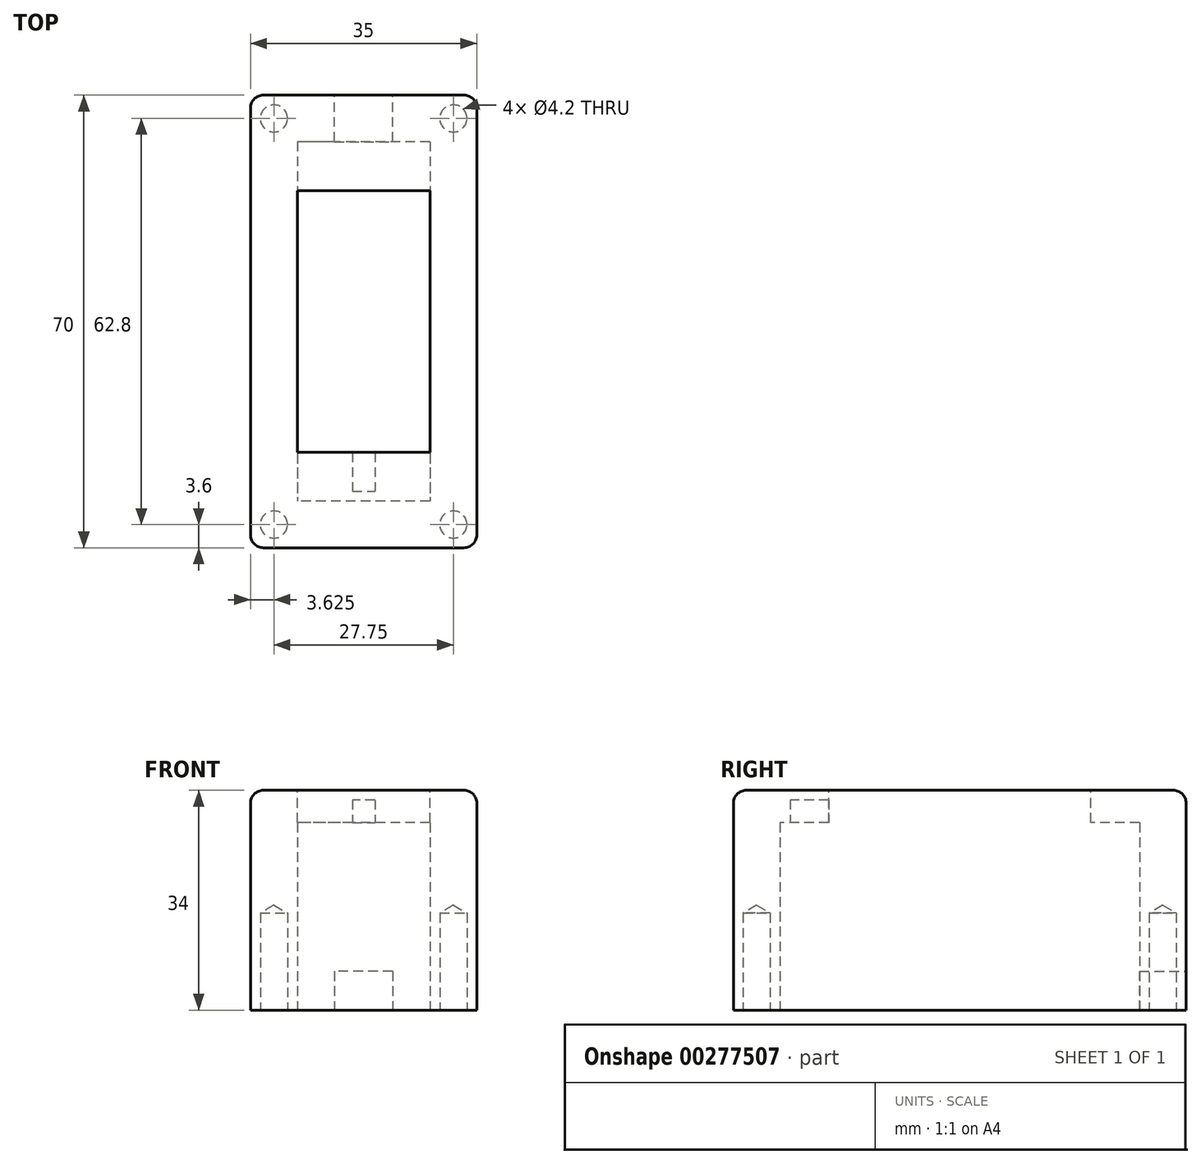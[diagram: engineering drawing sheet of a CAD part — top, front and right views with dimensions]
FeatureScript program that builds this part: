
annotation { "Feature Type Name" : "Feature", "Feature Type Description" : "" }
export const myFeature = defineFeature(function(context is Context, id is Id, definition is map)
    precondition{}
    {
        {
            var Q0;
            Q0=qCreatedBy(makeId("Top.planeOp"),FACE);
            var sketch = newSketch(context, id + "F0", { "sketchPlane" : qUnion([Q0])});
            skLineSegment(sketch, "E0.bottom", {"start": v(17.5, 35) * mm, "end": v(-17.5, 35) * mm});
            skLineSegment(sketch, "E0.top", {"start": v(17.5, -35) * mm, "end": v(-17.5, -35) * mm});
            skLineSegment(sketch, "E0.left", {"start": v(17.5, 35) * mm, "end": v(17.5, -35) * mm});
            skLineSegment(sketch, "E0.right", {"start": v(-17.5, 35) * mm, "end": v(-17.5, -35) * mm});
            skPoint(sketch, "E0.middle", {"position": v(0, 0) * mm});
            skSolve(sketch);
        }
        {
            var Q0;
            Q0=makeQuery(id+"F0.imprint","IMPRINT",FACE,{"disambiguationData":[TD([[makeQuery(id+"F0.imprint","IMPRINT",EDGE,{"derivedFrom":sQuery(id+"F0.wireOp",EDGE,"E0.bottom")}),1.0]])]});
            extrude(context, id + "F1", {"entities" : qUnion([Q0]), "depth" : 40 * mm});
        }
        {
            var Q0;
            Q0=makeQuery(id+"F1.opExtrude","CAP_FACE",FACE,{"disambiguationData":[OSD([sQuery(id+"F0.wireOp",EDGE,"E0.bottom"),sQuery(id+"F0.wireOp",EDGE,"E0.top"),sQuery(id+"F0.wireOp",EDGE,"E0.left"),sQuery(id+"F0.wireOp",EDGE,"E0.right")])],"isStart":true});
            var sketch = newSketch(context, id + "F2", { "sketchPlane" : qUnion([Q0])});
            skLineSegment(sketch, "E1.bottom", {"start": v(10.25, -27.8) * mm, "end": v(-10.25, -27.8) * mm});
            skLineSegment(sketch, "E1.top", {"start": v(10.25, 27.8) * mm, "end": v(-10.25, 27.8) * mm});
            skLineSegment(sketch, "E1.left", {"start": v(10.25, -27.8) * mm, "end": v(10.25, 27.8) * mm});
            skLineSegment(sketch, "E1.right", {"start": v(-10.25, -27.8) * mm, "end": v(-10.25, 27.8) * mm});
            skPoint(sketch, "E1.middle", {"position": v(0, 0) * mm});
            skSolve(sketch);
        }
        {
            var Q0;
            Q0=makeQuery(id+"F2.imprint","IMPRINT",FACE,{"disambiguationData":[TD([[makeQuery(id+"F2.imprint","IMPRINT",EDGE,{"derivedFrom":sQuery(id+"F2.wireOp",EDGE,"E1.bottom")}),-1.0]])]});
            extrude(context, id + "F3", {"entities" : qUnion([Q0]), "operationType" : NewBodyOperationType.REMOVE, "oppositeDirection" : true, "depth" : 35 * mm});
        }
        {
            var Q0;
            Q0=makeQuery(id+"F1.opExtrude","CAP_FACE",FACE,{"disambiguationData":[OSD([sQuery(id+"F0.wireOp",EDGE,"E0.bottom"),sQuery(id+"F0.wireOp",EDGE,"E0.top"),sQuery(id+"F0.wireOp",EDGE,"E0.left"),sQuery(id+"F0.wireOp",EDGE,"E0.right")])],"isStart":false});
            var sketch = newSketch(context, id + "F4", { "sketchPlane" : qUnion([Q0])});
            skLineSegment(sketch, "E2.bottom", {"start": v(-10.25, 20.25) * mm, "end": v(10.25, 20.25) * mm});
            skLineSegment(sketch, "E2.top", {"start": v(-10.25, -20.25) * mm, "end": v(10.25, -20.25) * mm});
            skLineSegment(sketch, "E2.left", {"start": v(-10.25, 20.25) * mm, "end": v(-10.25, -20.25) * mm});
            skLineSegment(sketch, "E2.right", {"start": v(10.25, 20.25) * mm, "end": v(10.25, -20.25) * mm});
            skPoint(sketch, "E2.middle", {"position": v(0, 0) * mm});
            skSolve(sketch);
        }
        {
            var Q0;
            Q0=makeQuery(id+"F4.imprint","IMPRINT",FACE,{"disambiguationData":[TD([[makeQuery(id+"F4.imprint","IMPRINT",EDGE,{"derivedFrom":sQuery(id+"F4.wireOp",EDGE,"E2.bottom")}),-1.0]])]});
            extrude(context, id + "F5", {"entities" : qUnion([Q0]), "operationType" : NewBodyOperationType.REMOVE, "oppositeDirection" : true, "depth" : 25 * mm});
        }
        {
            var Q0;
            Q0=makeQuery(id+"F1.opExtrude","CAP_FACE",FACE,{"disambiguationData":[OSD([sQuery(id+"F0.wireOp",EDGE,"E0.bottom"),sQuery(id+"F0.wireOp",EDGE,"E0.top"),sQuery(id+"F0.wireOp",EDGE,"E0.left"),sQuery(id+"F0.wireOp",EDGE,"E0.right")])],"isStart":true});
            extrude(context, id + "F6", {"entities" : qUnion([Q0]), "operationType" : NewBodyOperationType.REMOVE, "oppositeDirection" : true, "depth" : 6 * mm});
        }
        {
            var Q0;
            {var subQ0=sQuery(id+"F2.wireOp",EDGE,"E1.right");var subQ1=sQuery(id+"F2.wireOp",EDGE,"E1.left");var subQ2=sQuery(id+"F2.wireOp",EDGE,"E1.top");Q0=makeQuery(id+"F5.boolean.opBoolean","SPLIT",FACE,{"disambiguationData":[TD([makeQuery(id+"F3.boolean.opBoolean","COPY",FACE,{"derivedFrom":makeQuery(id+"F3.opExtrude","SWEPT_FACE",FACE,{"disambiguationData":[OSD([subQ2])]})})])],"derivedFrom":makeQuery(id+"F3.boolean.opBoolean","COPY",FACE,{"derivedFrom":makeQuery(id+"F3.opExtrude","CAP_FACE",FACE,{"disambiguationData":[OSD([sQuery(id+"F2.wireOp",EDGE,"E1.bottom"),subQ2,subQ1,subQ0])],"isStart":false})})});}
            var sketch = newSketch(context, id + "F7", { "sketchPlane" : qUnion([Q0])});
            skLineSegment(sketch, "E3.bottom", {"start": v(1.75, 20.25) * mm, "end": v(-1.75, 20.25) * mm});
            skLineSegment(sketch, "E3.top", {"start": v(1.75, 35.35) * mm, "end": v(-1.75, 35.35) * mm});
            skLineSegment(sketch, "E3.left", {"start": v(1.75, 20.25) * mm, "end": v(1.75, 35.35) * mm});
            skLineSegment(sketch, "E3.right", {"start": v(-1.75, 20.25) * mm, "end": v(-1.75, 35.35) * mm});
            skPoint(sketch, "E3.middle", {"position": v(0, 27.8) * mm});
            skLineSegment(sketch, "E4", {"start": v(-1.75, 26.25) * mm, "end": v(1.75, 26.25) * mm});
            skSolve(sketch);
        }
        {
            var Q0;
            {var subQ0=sQuery(id+"F7.wireOp",EDGE,"E3.bottom");Q0=makeQuery(id+"F7.imprint","IMPRINT",FACE,{"disambiguationData":[TD([[makeQuery(id+"F7.imprint","IMPRINT",EDGE,{"derivedFrom":subQ0}),-1.0]])]});}
            extrude(context, id + "F8", {"entities" : qUnion([Q0]), "operationType" : NewBodyOperationType.REMOVE, "oppositeDirection" : true, "depth" : 3.5 * mm});
        }
        {
            var Q0;
            Q0=makeQuery(id+"F6.boolean.opBoolean","COPY",FACE,{"derivedFrom":makeQuery(id+"F6.opExtrude","CAP_FACE",FACE,{"disambiguationData":[OSD([sQuery(id+"F0.wireOp",EDGE,"E0.bottom"),sQuery(id+"F0.wireOp",EDGE,"E0.top"),sQuery(id+"F0.wireOp",EDGE,"E0.left"),sQuery(id+"F0.wireOp",EDGE,"E0.right")])],"isStart":false})});
            var sketch = newSketch(context, id + "F9", { "sketchPlane" : qUnion([Q0])});
            skLineSegment(sketch, "E5", {"start": v(10.25, 27.8) * mm, "end": v(17.5, 35) * mm});
            skLineSegment(sketch, "E6", {"start": v(-17.5, 35) * mm, "end": v(-10.25, 27.8) * mm});
            skLineSegment(sketch, "E7", {"start": v(-17.5, -35) * mm, "end": v(-10.25, -27.8) * mm});
            skLineSegment(sketch, "E8", {"start": v(10.25, -27.8) * mm, "end": v(17.5, -35) * mm});
            skPoint(sketch, "E9", {"position": v(-13.88, 31.4) * mm});
            skPoint(sketch, "E10", {"position": v(13.87, 31.4) * mm});
            skPoint(sketch, "E11", {"position": v(13.88, -31.4) * mm});
            skPoint(sketch, "E12", {"position": v(-13.87, -31.4) * mm});
            skSolve(sketch);
        }
        {
            var Q0;
            Q0=sQuery(id+"F9.wireOp",VERTEX,"E9");
            var Q1;
            Q1=sQuery(id+"F9.wireOp",VERTEX,"E10");
            var Q2;
            Q2=sQuery(id+"F9.wireOp",VERTEX,"E11");
            var Q3;
            Q3=sQuery(id+"F9.wireOp",VERTEX,"E12");
            var Q4;
            Q4=makeQuery(id+"F1.opExtrude","SWEPT_BODY",BODY,{"disambiguationData":[OSD([sQuery(id+"F0.wireOp",EDGE,"E0.bottom"),sQuery(id+"F0.wireOp",EDGE,"E0.top"),sQuery(id+"F0.wireOp",EDGE,"E0.left"),sQuery(id+"F0.wireOp",EDGE,"E0.right")])]});
            hole(context, id + "F10", {"style" : HoleStyle.SIMPLE, "endStyle" : HoleEndStyle.BLIND, "holeDiameter" : 4.2 * mm, "holeDepth" : 15 * mm, "tappedDepth" : 12 * mm, "tapClearance" : 3, "locations" : qUnion([Q0, Q1, Q2, Q3]), "scope" : qUnion([Q4])});
        }
        {
            var Q0;
            Q0=makeQuery(id+"F1.opExtrude","SWEPT_EDGE",EDGE,{"disambiguationData":[OSD([sQuery(id+"F0.wireOp",EDGE,"E0.top"),sQuery(id+"F0.wireOp",EDGE,"E0.left")])]});
            var Q1;
            Q1=makeQuery(id+"F1.opExtrude","CAP_EDGE",EDGE,{"disambiguationData":[OSD([sQuery(id+"F0.wireOp",EDGE,"E0.left")])],"isStart":false});
            var Q2;
            Q2=makeQuery(id+"F1.opExtrude","CAP_EDGE",EDGE,{"disambiguationData":[OSD([sQuery(id+"F0.wireOp",EDGE,"E0.top")])],"isStart":false});
            var Q3;
            Q3=makeQuery(id+"F1.opExtrude","CAP_EDGE",EDGE,{"disambiguationData":[OSD([sQuery(id+"F0.wireOp",EDGE,"E0.right")])],"isStart":false});
            var Q4;
            Q4=makeQuery(id+"F1.opExtrude","SWEPT_EDGE",EDGE,{"disambiguationData":[OSD([sQuery(id+"F0.wireOp",EDGE,"E0.bottom"),sQuery(id+"F0.wireOp",EDGE,"E0.left")])]});
            var Q5;
            Q5=makeQuery(id+"F1.opExtrude","CAP_EDGE",EDGE,{"disambiguationData":[OSD([sQuery(id+"F0.wireOp",EDGE,"E0.bottom")])],"isStart":false});
            var Q6;
            Q6=makeQuery(id+"F1.opExtrude","SWEPT_EDGE",EDGE,{"disambiguationData":[OSD([sQuery(id+"F0.wireOp",EDGE,"E0.top"),sQuery(id+"F0.wireOp",EDGE,"E0.right")])]});
            var Q7;
            Q7=makeQuery(id+"F1.opExtrude","SWEPT_EDGE",EDGE,{"disambiguationData":[OSD([sQuery(id+"F0.wireOp",EDGE,"E0.bottom"),sQuery(id+"F0.wireOp",EDGE,"E0.right")])]});
            fillet(context, id + "F11", {"entities" : qUnion([Q0, Q1, Q2, Q3, Q4, Q5, Q6, Q7]), "radius" : 2 * mm, "tangentPropagation" : true, "allowEdgeOverflow" : false});
        }
        {
            var Q0;
            Q0=makeQuery(id+"F1.opExtrude","SWEPT_FACE",FACE,{"disambiguationData":[OSD([sQuery(id+"F0.wireOp",EDGE,"E0.bottom")])]});
            var sketch = newSketch(context, id + "F12", { "sketchPlane" : qUnion([Q0])});
            skLineSegment(sketch, "E13.bottom", {"start": v(-4.5, 12) * mm, "end": v(4.5, 12) * mm});
            skLineSegment(sketch, "E13.top", {"start": v(-4.5, 0) * mm, "end": v(4.5, 0) * mm});
            skLineSegment(sketch, "E13.left", {"start": v(-4.5, 12) * mm, "end": v(-4.5, 0) * mm});
            skLineSegment(sketch, "E13.right", {"start": v(4.5, 12) * mm, "end": v(4.5, 0) * mm});
            skPoint(sketch, "E13.middle", {"position": v(0, 6) * mm});
            skLineSegment(sketch, "E14", {"start": v(4.5, 6) * mm, "end": v(-4.5, 6) * mm});
            skSolve(sketch);
        }
        {
            var Q0;
            {var subQ0=sQuery(id+"F12.wireOp",EDGE,"E13.bottom");Q0=makeQuery(id+"F12.imprint","IMPRINT",FACE,{"disambiguationData":[TD([[makeQuery(id+"F12.imprint","IMPRINT",EDGE,{"derivedFrom":subQ0}),-1.0]])]});}
            extrude(context, id + "F13", {"entities" : qUnion([Q0]), "operationType" : NewBodyOperationType.REMOVE, "oppositeDirection" : true, "depth" : 10 * mm});
        }
    });
